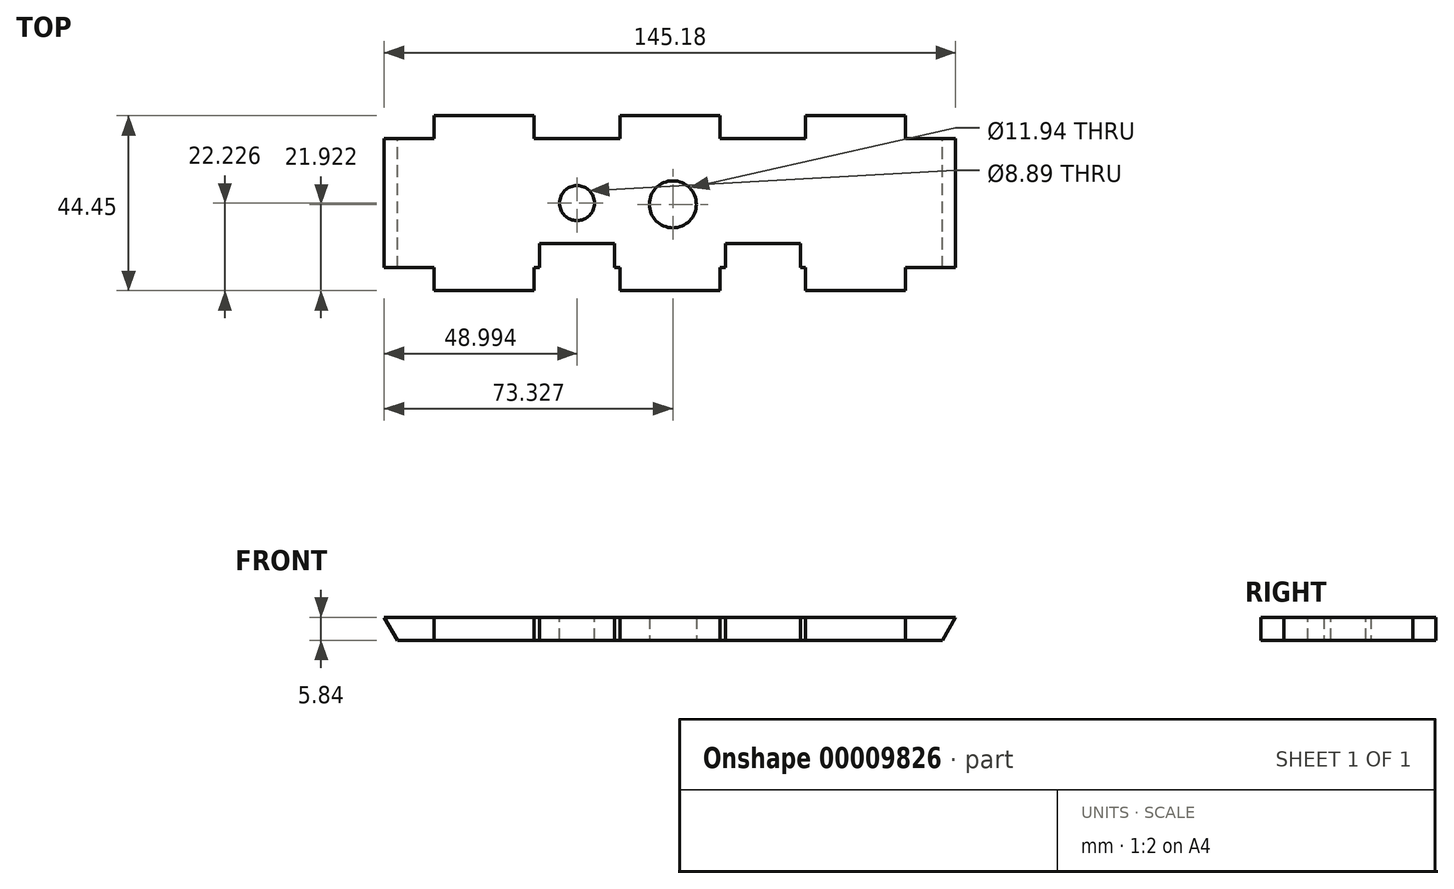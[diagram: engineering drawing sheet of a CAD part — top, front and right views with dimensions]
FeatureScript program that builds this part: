
annotation { "Feature Type Name" : "Feature", "Feature Type Description" : "" }
export const myFeature = defineFeature(function(context is Context, id is Id, definition is map)
    precondition{}
    {
        {
            var Q0;
            Q0=qCreatedBy(makeId("Top.planeOp"),FACE);
            var sketch = newSketch(context, id + "F0", { "sketchPlane" : qUnion([Q0])});
            skLineSegment(sketch, "E0.bottom", {"start": v(-125.55, -13.09) * mm, "end": v(19.63, -13.09) * mm});
            skLineSegment(sketch, "E0.top", {"start": v(-125.55, -57.54) * mm, "end": v(19.63, -57.54) * mm});
            skLineSegment(sketch, "E0.left", {"start": v(-125.55, -13.09) * mm, "end": v(-125.55, -57.54) * mm});
            skLineSegment(sketch, "E0.right", {"start": v(19.63, -13.09) * mm, "end": v(19.63, -57.54) * mm});
            skSolve(sketch);
        }
        {
            var Q0;
            Q0 = qSketchRegion(id + "F0", true);
            extrude(context, id + "F1", {"entities" : qUnion([Q0]), "depth" : 5.84 * mm});
        }
        {
            var Q0;
            Q0=makeQuery(id+"F1.opExtrude","CAP_FACE",FACE,{"disambiguationData":[OSD([sQuery(id+"F0.wireOp",EDGE,"E0.bottom"),sQuery(id+"F0.wireOp",EDGE,"E0.top"),sQuery(id+"F0.wireOp",EDGE,"E0.left"),sQuery(id+"F0.wireOp",EDGE,"E0.right")])],"isStart":false});
            var sketch = newSketch(context, id + "F2", { "sketchPlane" : qUnion([Q0])});
            skLineSegment(sketch, "E1.bottom", {"start": v(-112.85, -13.09) * mm, "end": v(-87.45, -13.09) * mm});
            skLineSegment(sketch, "E1.left", {"start": v(-112.85, -13.09) * mm, "end": v(-112.85, -18.93) * mm});
            skLineSegment(sketch, "E1.right", {"start": v(-87.45, -13.09) * mm, "end": v(-87.45, -18.93) * mm});
            skLineSegment(sketch, "E2.bottom", {"start": v(-65.66, -13.09) * mm, "end": v(-40.26, -13.09) * mm});
            skLineSegment(sketch, "E2.left", {"start": v(-65.66, -13.09) * mm, "end": v(-65.66, -18.93) * mm});
            skLineSegment(sketch, "E2.right", {"start": v(-40.26, -13.09) * mm, "end": v(-40.26, -18.93) * mm});
            skLineSegment(sketch, "E3.bottom", {"start": v(-18.47, -13.09) * mm, "end": v(6.93, -13.09) * mm});
            skLineSegment(sketch, "E3.left", {"start": v(-18.47, -13.09) * mm, "end": v(-18.47, -18.93) * mm});
            skLineSegment(sketch, "E3.right", {"start": v(6.93, -13.09) * mm, "end": v(6.93, -18.93) * mm});
            skLineSegment(sketch, "E4.bottom", {"start": v(-112.85, -57.54) * mm, "end": v(-87.45, -57.54) * mm});
            skLineSegment(sketch, "E4.left", {"start": v(-112.85, -57.54) * mm, "end": v(-112.85, -51.7) * mm});
            skLineSegment(sketch, "E4.right", {"start": v(-87.45, -57.54) * mm, "end": v(-87.45, -51.7) * mm});
            skLineSegment(sketch, "E5.bottom", {"start": v(-65.66, -57.54) * mm, "end": v(-40.26, -57.54) * mm});
            skLineSegment(sketch, "E5.left", {"start": v(-65.66, -57.54) * mm, "end": v(-65.66, -51.7) * mm});
            skLineSegment(sketch, "E5.right", {"start": v(-40.26, -57.54) * mm, "end": v(-40.26, -51.7) * mm});
            skLineSegment(sketch, "E6.bottom", {"start": v(-18.47, -57.54) * mm, "end": v(6.93, -57.54) * mm});
            skLineSegment(sketch, "E6.left", {"start": v(-18.47, -57.54) * mm, "end": v(-18.47, -51.7) * mm});
            skLineSegment(sketch, "E6.right", {"start": v(6.93, -57.54) * mm, "end": v(6.93, -51.7) * mm});
            skPoint(sketch, "E7", {"position": v(-52.96, -18.93) * mm});
            skPoint(sketch, "E8", {"position": v(-52.96, -51.7) * mm});
            skLineSegment(sketch, "E9", {"start": v(-112.85, -18.93) * mm, "end": v(-125.55, -18.93) * mm});
            skLineSegment(sketch, "E10", {"start": v(-112.85, -51.7) * mm, "end": v(-125.55, -51.7) * mm});
            skLineSegment(sketch, "E11", {"start": v(-125.55, -51.7) * mm, "end": v(-125.55, -18.93) * mm});
            skLineSegment(sketch, "E12", {"start": v(6.93, -18.93) * mm, "end": v(19.63, -18.93) * mm});
            skLineSegment(sketch, "E13", {"start": v(6.93, -51.7) * mm, "end": v(19.63, -51.7) * mm});
            skLineSegment(sketch, "E14", {"start": v(19.63, -51.7) * mm, "end": v(19.63, -18.93) * mm});
            skLineSegment(sketch, "E15", {"start": v(-87.45, -18.93) * mm, "end": v(-65.66, -18.93) * mm});
            skLineSegment(sketch, "E16", {"start": v(-40.26, -18.93) * mm, "end": v(-18.47, -18.93) * mm});
            skLineSegment(sketch, "E17", {"start": v(-18.47, -51.7) * mm, "end": v(-40.26, -51.7) * mm});
            skLineSegment(sketch, "E18", {"start": v(-65.66, -51.7) * mm, "end": v(-87.45, -51.7) * mm});
            skSolve(sketch);
        }
        {
            var Q0;
            {var subQ4=sQuery(id+"F2.wireOp",EDGE,"E1.left");Q0=makeQuery(id+"F2.imprint","IMPRINT",FACE,{"disambiguationData":[TD([[makeQuery(id+"F2.imprint","IMPRINT",EDGE,{"derivedFrom":subQ4}),-1.0]])]});}
            var Q1;
            {var subQ2=sQuery(id+"F2.wireOp",EDGE,"E1.right");Q1=makeQuery(id+"F2.imprint","IMPRINT",FACE,{"disambiguationData":[TD([[makeQuery(id+"F2.imprint","IMPRINT",EDGE,{"derivedFrom":subQ2}),1.0]])]});}
            var Q2;
            {var subQ2=sQuery(id+"F2.wireOp",EDGE,"E2.right");Q2=makeQuery(id+"F2.imprint","IMPRINT",FACE,{"disambiguationData":[TD([[makeQuery(id+"F2.imprint","IMPRINT",EDGE,{"derivedFrom":subQ2}),1.0]])]});}
            var Q3;
            {var subQ4=sQuery(id+"F2.wireOp",EDGE,"E3.right");Q3=makeQuery(id+"F2.imprint","IMPRINT",FACE,{"disambiguationData":[TD([[makeQuery(id+"F2.imprint","IMPRINT",EDGE,{"derivedFrom":subQ4}),1.0]])]});}
            var Q4;
            {var subQ4=sQuery(id+"F2.wireOp",EDGE,"E6.right");Q4=makeQuery(id+"F2.imprint","IMPRINT",FACE,{"disambiguationData":[TD([[makeQuery(id+"F2.imprint","IMPRINT",EDGE,{"derivedFrom":subQ4}),-1.0]])]});}
            var Q5;
            {var subQ2=sQuery(id+"F2.wireOp",EDGE,"E5.right");Q5=makeQuery(id+"F2.imprint","IMPRINT",FACE,{"disambiguationData":[TD([[makeQuery(id+"F2.imprint","IMPRINT",EDGE,{"derivedFrom":subQ2}),-1.0]])]});}
            var Q6;
            {var subQ2=sQuery(id+"F2.wireOp",EDGE,"E4.right");Q6=makeQuery(id+"F2.imprint","IMPRINT",FACE,{"disambiguationData":[TD([[makeQuery(id+"F2.imprint","IMPRINT",EDGE,{"derivedFrom":subQ2}),-1.0]])]});}
            var Q7;
            {var subQ4=sQuery(id+"F2.wireOp",EDGE,"E4.left");Q7=makeQuery(id+"F2.imprint","IMPRINT",FACE,{"disambiguationData":[TD([[makeQuery(id+"F2.imprint","IMPRINT",EDGE,{"derivedFrom":subQ4}),1.0]])]});}
            var Q8;
            Q8=makeQuery(id+"F1.opExtrude","CAP_FACE",FACE,{"disambiguationData":[OSD([sQuery(id+"F0.wireOp",EDGE,"E0.bottom"),sQuery(id+"F0.wireOp",EDGE,"E0.top"),sQuery(id+"F0.wireOp",EDGE,"E0.left"),sQuery(id+"F0.wireOp",EDGE,"E0.right")])],"isStart":false});
            extrude(context, id + "F3", {"entities" : qUnion([Q0, Q1, Q2, Q3, Q4, Q5, Q6, Q7]), "operationType" : NewBodyOperationType.REMOVE, "endBound" : BoundingType.THROUGH_ALL, "oppositeDirection" : true, "endBoundEntityFace" : qUnion([Q8]), "depth" : 25.4 * mm});
        }
        {
            var Q0;
            Q0=makeQuery(id+"F1.opExtrude","CAP_FACE",FACE,{"disambiguationData":[OSD([sQuery(id+"F0.wireOp",EDGE,"E0.bottom"),sQuery(id+"F0.wireOp",EDGE,"E0.top"),sQuery(id+"F0.wireOp",EDGE,"E0.left"),sQuery(id+"F0.wireOp",EDGE,"E0.right")])],"isStart":true});
            var sketch = newSketch(context, id + "F4", { "sketchPlane" : qUnion([Q0])});
            skCircle(sketch, "E19", {"center": v(-52.22, 35.62) * mm, "radius": 5.97 * mm});
            skSolve(sketch);
        }
        {
            var Q0;
            Q0=makeQuery(id+"F4.imprint","IMPRINT",FACE,{"disambiguationData":[TD([[makeQuery(id+"F4.imprint","IMPRINT",EDGE,{"derivedFrom":sQuery(id+"F4.wireOp",EDGE,"E19")}),1.0]])]});
            extrude(context, id + "F5", {"entities" : qUnion([Q0]), "operationType" : NewBodyOperationType.REMOVE, "endBound" : BoundingType.THROUGH_ALL, "oppositeDirection" : true, "depth" : 25.4 * mm});
        }
        {
            var Q0;
            Q0=makeQuery(id+"F1.opExtrude","CAP_FACE",FACE,{"disambiguationData":[OSD([sQuery(id+"F0.wireOp",EDGE,"E0.bottom"),sQuery(id+"F0.wireOp",EDGE,"E0.top"),sQuery(id+"F0.wireOp",EDGE,"E0.left"),sQuery(id+"F0.wireOp",EDGE,"E0.right")])],"isStart":false});
            var sketch = newSketch(context, id + "F6", { "sketchPlane" : qUnion([Q0])});
            skLineSegment(sketch, "E20.bottom", {"start": v(-86.08, -45.6) * mm, "end": v(-67.03, -45.6) * mm});
            skLineSegment(sketch, "E20.top", {"start": v(-86.08, -51.7) * mm, "end": v(-67.03, -51.7) * mm});
            skLineSegment(sketch, "E20.left", {"start": v(-86.08, -45.6) * mm, "end": v(-86.08, -51.7) * mm});
            skLineSegment(sketch, "E20.right", {"start": v(-67.03, -45.6) * mm, "end": v(-67.03, -51.7) * mm});
            skPoint(sketch, "E21", {"position": v(-76.56, -45.6) * mm});
            skLineSegment(sketch, "E22.bottom", {"start": v(-38.89, -45.6) * mm, "end": v(-19.84, -45.6) * mm});
            skLineSegment(sketch, "E22.top", {"start": v(-38.89, -51.7) * mm, "end": v(-19.84, -51.7) * mm});
            skLineSegment(sketch, "E22.left", {"start": v(-38.89, -45.6) * mm, "end": v(-38.89, -51.7) * mm});
            skLineSegment(sketch, "E22.right", {"start": v(-19.84, -45.6) * mm, "end": v(-19.84, -51.7) * mm});
            skPoint(sketch, "E23", {"position": v(-29.36, -51.7) * mm});
            skPoint(sketch, "E24", {"position": v(-76.56, -51.7) * mm});
            skSolve(sketch);
        }
        {
            var Q0;
            Q0=makeQuery(id+"F6.imprint","IMPRINT",FACE,{"disambiguationData":[TD([[makeQuery(id+"F6.imprint","IMPRINT",EDGE,{"derivedFrom":sQuery(id+"F6.wireOp",EDGE,"E20.bottom")}),-1.0]])]});
            var Q1;
            Q1=makeQuery(id+"F6.imprint","IMPRINT",FACE,{"disambiguationData":[TD([[makeQuery(id+"F6.imprint","IMPRINT",EDGE,{"derivedFrom":sQuery(id+"F6.wireOp",EDGE,"E22.bottom")}),-1.0]])]});
            extrude(context, id + "F7", {"entities" : qUnion([Q0, Q1]), "operationType" : NewBodyOperationType.REMOVE, "endBound" : BoundingType.THROUGH_ALL, "oppositeDirection" : true, "depth" : 25.4 * mm});
        }
        {
            var Q0;
            Q0=makeQuery(id+"F3.boolean.opBoolean","COPY",FACE,{"derivedFrom":makeQuery(id+"F3.opExtrude","SWEPT_FACE",FACE,{"disambiguationData":[OSD([sQuery(id+"F2.wireOp",EDGE,"E12")])]})});
            var sketch = newSketch(context, id + "F8", { "sketchPlane" : qUnion([Q0])});
            skLineSegment(sketch, "E25", {"start": v(-19.63, 5.84) * mm, "end": v(-16.26, 0) * mm});
            skLineSegment(sketch, "E26", {"start": v(-16.26, 0) * mm, "end": v(-16.26, 5.84) * mm});
            skLineSegment(sketch, "E27", {"start": v(-16.26, 5.84) * mm, "end": v(-19.63, 5.84) * mm});
            skSolve(sketch);
        }
        {
            var Q0;
            Q0=makeQuery(id+"F3.boolean.opBoolean","COPY",FACE,{"derivedFrom":makeQuery(id+"F3.opExtrude","SWEPT_FACE",FACE,{"disambiguationData":[OSD([sQuery(id+"F2.wireOp",EDGE,"E9")])]})});
            var sketch = newSketch(context, id + "F9", { "sketchPlane" : qUnion([Q0])});
            skLineSegment(sketch, "E28", {"start": v(125.55, 5.84) * mm, "end": v(122.18, 0) * mm});
            skLineSegment(sketch, "E29", {"start": v(122.18, 0) * mm, "end": v(122.18, 5.84) * mm});
            skLineSegment(sketch, "E30", {"start": v(122.18, 5.84) * mm, "end": v(125.55, 5.84) * mm});
            skSolve(sketch);
        }
        {
            var Q0;
            {var subQ3=sQuery(id+"F9.wireOp",EDGE,"E28");Q0=makeQuery(id+"F9.imprint","IMPRINT",FACE,{"disambiguationData":[TD([[makeQuery(id+"F9.imprint","IMPRINT",EDGE,{"derivedFrom":subQ3}),1.0]])]});}
            var Q1;
            {var subQ3=sQuery(id+"F8.wireOp",EDGE,"E25");Q1=makeQuery(id+"F8.imprint","IMPRINT",FACE,{"disambiguationData":[TD([[makeQuery(id+"F8.imprint","IMPRINT",EDGE,{"derivedFrom":subQ3}),-1.0]])]});}
            extrude(context, id + "F10", {"entities" : qUnion([Q0, Q1]), "operationType" : NewBodyOperationType.REMOVE, "endBound" : BoundingType.THROUGH_ALL, "oppositeDirection" : true, "depth" : 25.4 * mm});
        }
        {
            var Q0;
            Q0=makeQuery(id+"F1.opExtrude","CAP_FACE",FACE,{"disambiguationData":[OSD([sQuery(id+"F0.wireOp",EDGE,"E0.bottom"),sQuery(id+"F0.wireOp",EDGE,"E0.top"),sQuery(id+"F0.wireOp",EDGE,"E0.left"),sQuery(id+"F0.wireOp",EDGE,"E0.right")])],"isStart":false});
            var sketch = newSketch(context, id + "F11", { "sketchPlane" : qUnion([Q0])});
            skCircle(sketch, "E31", {"center": v(-76.56, -35.31) * mm, "radius": 4.45 * mm});
            skPoint(sketch, "E32", {"position": v(-76.56, -18.93) * mm});
            skSolve(sketch);
        }
        {
            var Q0;
            Q0=makeQuery(id+"F11.imprint","IMPRINT",FACE,{"disambiguationData":[TD([[makeQuery(id+"F11.imprint","IMPRINT",EDGE,{"derivedFrom":sQuery(id+"F11.wireOp",EDGE,"E31")}),1.0]])]});
            var Q1;
            Q1=makeQuery(id+"F1.opExtrude","CAP_FACE",FACE,{"disambiguationData":[OSD([sQuery(id+"F0.wireOp",EDGE,"E0.bottom"),sQuery(id+"F0.wireOp",EDGE,"E0.top"),sQuery(id+"F0.wireOp",EDGE,"E0.left"),sQuery(id+"F0.wireOp",EDGE,"E0.right")])],"isStart":true});
            extrude(context, id + "F12", {"entities" : qUnion([Q0]), "operationType" : NewBodyOperationType.REMOVE, "endBound" : BoundingType.UP_TO_SURFACE, "oppositeDirection" : true, "endBoundEntityFace" : qUnion([Q1]), "depth" : 25.4 * mm});
        }
    });
